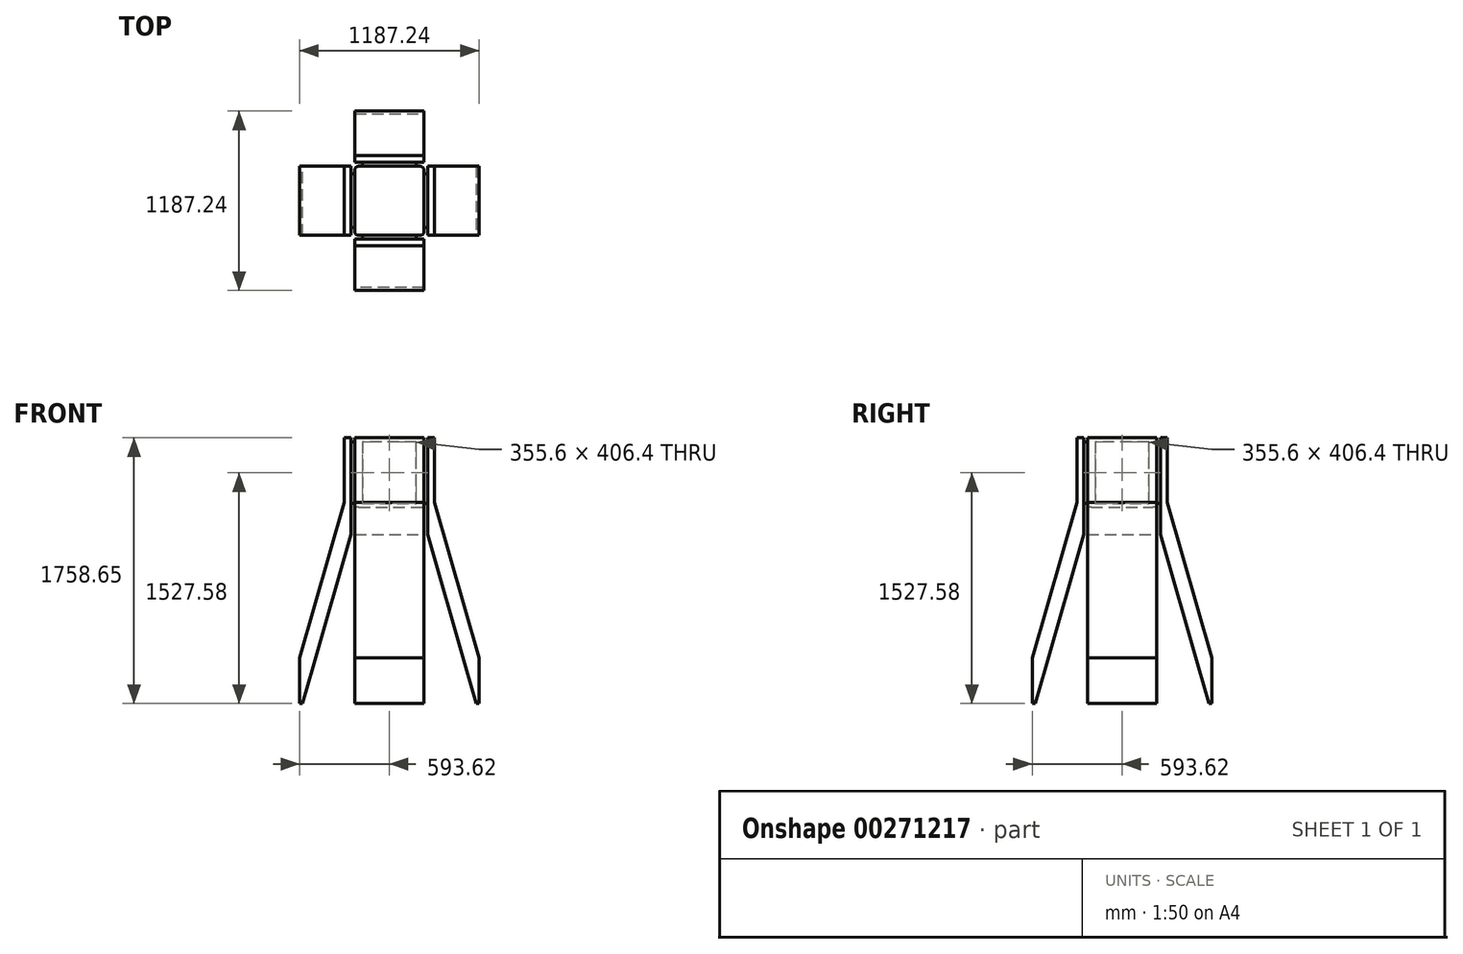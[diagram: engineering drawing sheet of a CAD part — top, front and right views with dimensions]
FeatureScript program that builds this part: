
annotation { "Feature Type Name" : "Feature", "Feature Type Description" : "" }
export const myFeature = defineFeature(function(context is Context, id is Id, definition is map)
    precondition{}
    {
        {
            var Q0;
            Q0=qCreatedBy(makeId("Top.planeOp"),FACE);
            var sketch = newSketch(context, id + "F0", { "sketchPlane" : qUnion([Q0])});
            skLineSegment(sketch, "E0.bottom", {"start": v(-203.2, -228.6) * mm, "end": v(203.2, -228.6) * mm});
            skLineSegment(sketch, "E0.top", {"start": v(-203.2, 228.6) * mm, "end": v(203.2, 228.6) * mm});
            skLineSegment(sketch, "E0.left", {"start": v(-228.6, -203.2) * mm, "end": v(-228.6, 203.2) * mm});
            skLineSegment(sketch, "E0.right", {"start": v(228.6, -203.2) * mm, "end": v(228.6, 203.2) * mm});
            skPoint(sketch, "E1.visualSharp", {"position": v(-228.6, -228.6) * mm});
            skArc(sketch, "E1.filletArc", {"start": v(-228.6, -203.2) * mm, "mid": v(-221.16, -221.16) * mm, "end": v(-203.2, -228.6) * mm});
            skPoint(sketch, "E2.visualSharp", {"position": v(-228.6, 228.6) * mm});
            skArc(sketch, "E2.filletArc", {"start": v(-203.2, 228.6) * mm, "mid": v(-221.16, 221.16) * mm, "end": v(-228.6, 203.2) * mm});
            skPoint(sketch, "E3.visualSharp", {"position": v(228.6, 228.6) * mm});
            skArc(sketch, "E3.filletArc", {"start": v(228.6, 203.2) * mm, "mid": v(221.16, 221.16) * mm, "end": v(203.2, 228.6) * mm});
            skPoint(sketch, "E4.visualSharp", {"position": v(228.6, -228.6) * mm});
            skArc(sketch, "E4.filletArc", {"start": v(203.2, -228.6) * mm, "mid": v(221.16, -221.16) * mm, "end": v(228.6, -203.2) * mm});
            skLineSegment(sketch, "E5", {"start": v(0, 228.6) * mm, "end": v(0, -228.6) * mm, "construction": true});
            skLineSegment(sketch, "E6", {"start": v(0, -228.6) * mm, "end": v(228.6, 0) * mm, "construction": true});
            skLineSegment(sketch, "E7", {"start": v(228.6, 0) * mm, "end": v(-228.6, 0) * mm, "construction": true});
            skPoint(sketch, "E8", {"position": v(0, 0) * mm});
            skSolve(sketch);
        }
        {
            var Q0;
            Q0 = qSketchRegion(id + "F0", true);
            extrude(context, id + "F1", {"entities" : qUnion([Q0]), "depth" : 457.2 * mm});
        }
        {
            var Q0;
            Q0=makeQuery(id+"F1.opExtrude","SWEPT_FACE",FACE,{"disambiguationData":[OSD([sQuery(id+"F0.wireOp",EDGE,"E0.right")])]});
            var sketch = newSketch(context, id + "F2", { "sketchPlane" : qUnion([Q0])});
            skLineSegment(sketch, "E9.0", {"start": v(-177.8, 25.4) * mm, "end": v(177.8, 25.4) * mm});
            skLineSegment(sketch, "E9.1", {"start": v(-177.8, 431.8) * mm, "end": v(-177.8, 25.4) * mm});
            skLineSegment(sketch, "E9.2", {"start": v(177.8, 431.8) * mm, "end": v(-177.8, 431.8) * mm});
            skLineSegment(sketch, "E9.3", {"start": v(177.8, 25.4) * mm, "end": v(177.8, 431.8) * mm});
            skSolve(sketch);
        }
        {
            var Q0;
            Q0 = qSketchRegion(id + "F2", true);
            extrude(context, id + "F3", {"entities" : qUnion([Q0]), "operationType" : NewBodyOperationType.ADD, "depth" : 25.4 * mm});
        }
        {
            var Q0;
            Q0=makeQuery(id+"F1.opExtrude","SWEPT_FACE",FACE,{"disambiguationData":[OSD([sQuery(id+"F0.wireOp",EDGE,"E0.bottom")])]});
            var sketch = newSketch(context, id + "F4", { "sketchPlane" : qUnion([Q0])});
            skLineSegment(sketch, "E10.0", {"start": v(-177.8, 25.4) * mm, "end": v(177.8, 25.4) * mm});
            skLineSegment(sketch, "E10.1", {"start": v(-177.8, 431.8) * mm, "end": v(-177.8, 25.4) * mm});
            skLineSegment(sketch, "E10.2", {"start": v(177.8, 431.8) * mm, "end": v(-177.8, 431.8) * mm});
            skLineSegment(sketch, "E10.3", {"start": v(177.8, 25.4) * mm, "end": v(177.8, 431.8) * mm});
            skSolve(sketch);
        }
        {
            var Q0;
            Q0=makeQuery(id+"F4.imprint","IMPRINT",FACE,{"disambiguationData":[TD([[makeQuery(id+"F4.imprint","IMPRINT",EDGE,{"derivedFrom":sQuery(id+"F4.wireOp",EDGE,"E10.0")}),1.0]])]});
            extrude(context, id + "F5", {"entities" : qUnion([Q0]), "operationType" : NewBodyOperationType.ADD, "depth" : 25.4 * mm});
        }
        {
            var Q0;
            Q0=makeQuery(id+"F1.opExtrude","SWEPT_FACE",FACE,{"disambiguationData":[OSD([sQuery(id+"F0.wireOp",EDGE,"E0.left")])]});
            var sketch = newSketch(context, id + "F6", { "sketchPlane" : qUnion([Q0])});
            skLineSegment(sketch, "E11.0", {"start": v(-177.8, 25.4) * mm, "end": v(177.8, 25.4) * mm});
            skLineSegment(sketch, "E11.1", {"start": v(-177.8, 431.8) * mm, "end": v(-177.8, 25.4) * mm});
            skLineSegment(sketch, "E11.2", {"start": v(177.8, 431.8) * mm, "end": v(-177.8, 431.8) * mm});
            skLineSegment(sketch, "E11.3", {"start": v(177.8, 25.4) * mm, "end": v(177.8, 431.8) * mm});
            skSolve(sketch);
        }
        {
            var Q0;
            Q0=makeQuery(id+"F6.imprint","IMPRINT",FACE,{"disambiguationData":[TD([[makeQuery(id+"F6.imprint","IMPRINT",EDGE,{"derivedFrom":sQuery(id+"F6.wireOp",EDGE,"E11.0")}),1.0]])]});
            extrude(context, id + "F7", {"entities" : qUnion([Q0]), "operationType" : NewBodyOperationType.ADD, "depth" : 25.4 * mm});
        }
        {
            var Q0;
            Q0=makeQuery(id+"F1.opExtrude","SWEPT_FACE",FACE,{"disambiguationData":[OSD([sQuery(id+"F0.wireOp",EDGE,"E0.top")])]});
            var sketch = newSketch(context, id + "F8", { "sketchPlane" : qUnion([Q0])});
            skLineSegment(sketch, "E12.0", {"start": v(-177.8, 25.4) * mm, "end": v(177.8, 25.4) * mm});
            skLineSegment(sketch, "E12.1", {"start": v(-177.8, 431.8) * mm, "end": v(-177.8, 25.4) * mm});
            skLineSegment(sketch, "E12.2", {"start": v(177.8, 431.8) * mm, "end": v(-177.8, 431.8) * mm});
            skLineSegment(sketch, "E12.3", {"start": v(177.8, 25.4) * mm, "end": v(177.8, 431.8) * mm});
            skSolve(sketch);
        }
        {
            var Q0;
            Q0=makeQuery(id+"F8.imprint","IMPRINT",FACE,{"disambiguationData":[TD([[makeQuery(id+"F8.imprint","IMPRINT",EDGE,{"derivedFrom":sQuery(id+"F8.wireOp",EDGE,"E12.0")}),1.0]])]});
            extrude(context, id + "F9", {"entities" : qUnion([Q0]), "operationType" : NewBodyOperationType.ADD, "depth" : 25.4 * mm});
        }
        {
            var Q0;
            Q0=qCreatedBy(makeId("Front.planeOp"),FACE);
            var sketch = newSketch(context, id + "F10", { "sketchPlane" : qUnion([Q0])});
            skPoint(sketch, "E13.0", {"position": v(-228.6, 457.2) * mm});
            skPoint(sketch, "E14.0", {"position": v(-254, 431.8) * mm});
            skLineSegment(sketch, "E15", {"start": v(-254, 459.67) * mm, "end": v(-254, -179.68) * mm});
            skPoint(sketch, "E16.end.orphan", {"position": v(-254, 529.82) * mm});
            skPoint(sketch, "E16.start.orphan", {"position": v(-313.82, 529.82) * mm});
            skLineSegment(sketch, "E17", {"start": v(-298.45, 33.9) * mm, "end": v(-298.45, 459.67) * mm});
            skPoint(sketch, "E18.start.orphan", {"position": v(-286.24, 459.67) * mm});
            skLineSegment(sketch, "E19", {"start": v(-298.45, 459.67) * mm, "end": v(-254, 459.67) * mm});
            skLineSegment(sketch, "E20.0", {"start": v(-593.62, -995.46) * mm, "end": v(-298.45, 33.9) * mm});
            skLineSegment(sketch, "E21.0", {"start": v(-505.6, -1057.1) * mm, "end": v(-254, -179.68) * mm});
            skLineSegment(sketch, "E22", {"start": v(-505.6, -1057.1) * mm, "end": v(-574.57, -1298.98) * mm});
            skLineSegment(sketch, "E23", {"start": v(-593.62, -1298.98) * mm, "end": v(-574.57, -1298.98) * mm});
            skPoint(sketch, "E24.orphan", {"position": v(-604.87, -1405.25) * mm});
            skPoint(sketch, "E25.orphan", {"position": v(-604.87, -1351.55) * mm});
            skPoint(sketch, "E26.orphan", {"position": v(-606.54, -1298.98) * mm});
            skLineSegment(sketch, "E27", {"start": v(-574.57, -1298.98) * mm, "end": v(-593.62, -1298.98) * mm});
            skLineSegment(sketch, "E28", {"start": v(-593.62, -1298.98) * mm, "end": v(-593.62, -995.46) * mm});
            skSolve(sketch);
        }
        {
            var Q0;
            Q0=makeQuery(id+"F10.imprint","IMPRINT",FACE,{"disambiguationData":[TD([[makeQuery(id+"F10.imprint","IMPRINT",EDGE,{"derivedFrom":sQuery(id+"F10.wireOp",EDGE,"E15")}),-1.0]])]});
            extrude(context, id + "F11", {"entities" : qUnion([Q0]), "endBound" : BoundingType.SYMMETRIC, "depth" : 457.2 * mm});
        }
        {
            var Q0;
            Q0=qCreatedBy(makeId("Front.planeOp"),FACE);
            var sketch = newSketch(context, id + "F12", { "sketchPlane" : qUnion([Q0])});
            skLineSegment(sketch, "E29", {"start": v(0, 0) * mm, "end": v(0, 306.95) * mm});
            skLineSegment(sketch, "E30", {"start": v(0, 306.95) * mm, "end": v(0, 256.25) * mm, "construction": true});
            skSolve(sketch);
        }
        {
            var Q0;
            Q0=makeQuery(id+"F11.opExtrude","SWEPT_BODY",BODY,{"disambiguationData":[OSD([sQuery(id+"F10.wireOp",EDGE,"E15"),sQuery(id+"F10.wireOp",EDGE,"E17"),sQuery(id+"F10.wireOp",EDGE,"E19"),sQuery(id+"F10.wireOp",EDGE,"E20.0"),sQuery(id+"F10.wireOp",EDGE,"E21.0"),sQuery(id+"F10.wireOp",EDGE,"E22"),sQuery(id+"F10.wireOp",EDGE,"E27"),sQuery(id+"F10.wireOp",EDGE,"E28")])]});
            var Q1;
            Q1=sQuery(id+"F12.wireOp",EDGE,"E29");
            circularPattern(context, id + "F13", {"entities" : qUnion([Q0]), "axis" : qUnion([Q1]), "angle" : 360 * degree, "instanceCount" : 4, "equalSpace" : true});
        }
    });
